# Revit family: 563622030037
name_source: partatom
category: Plumbing Fixtures
revit_build: Autodesk Revit 2017 (Build: 20190508_0315(x64)
units: mm (PartAtom-declared; Revit-internal decimal feet)

## family parameters
Always vertical = Yes
Cut with Voids When Loaded = No
OmniClass Number = 23.45.55.00
OmniClass Title = Sanitary Faucets, Wastes
Part Type = Normal
Room Calculation Point = No
Round Connector Dimension = Use Diameter
Shared = No
Work Plane-Based = No

## types (1)
- 563622030037 Washbasin faucet
    AssetType = Fixed
    BIMObjectName = 563622030037
    BodyMaterial = Brass
    Brand = Hansa
    Catalog Drawing URL = http://static.hansa.com
    Category = Bathroom
    Class = Single lever
    CloseOffRating = 0
    Color = Chrome
    Connection Size = G1/2
    ConvergoRefNr = 0087-1909-0142-FI
    Customs Code = 84818011
    DN Size = DN15
    Dimension Drawing URL = http://static.hansa.com
    DurationUnit = Year
    EAN Number = 4057304012068
    EN Standard = EN 817
    Extensions = Without popup waste
    FDV Document URL = http://www.hansa.com
    FaucetMainMaterial = Brass
    Features = Single lever
    Finish = Polished
    Flow Drawing URL = http://static.hansa.com
    Flow Rate At 300kPa With Flow Controller = 0.1 L/s
    FlowCoefficient = 0
    Group = Washbasin faucets
    IfcExportAs = IfcValveType
    IfcExportType = FAUCET
    InletConnectionSize = 10 mm  [stored 0.0328084 ft]
    Installation Type = Deck mounted
    Installation and Maintenance = http://static.hansa.com
    Lever Handle = Lever with H+C symbol
    ManufacterURL = http://www.hansa.com
    Manufacturer = Hansa
    ManufacturerName = Hansa
    Market = INT;AUS
    Material = Brass
    Max. Hot Water Supply = 90 °C
    Model = 563622030037 Washbasin faucet
    ModelReference = 563622030037
    Mounting Holes = 1 mounting hole
    NBSDescription = Water supply fittings for baths
    NBSReference = 45-35-70/315
    Name = 563622030037 Washbasin faucet
    Name_en = 563622030037 Washbasin faucet
    Noise Class = I (ISO 3822)
    NominalDepth = 137 mm
    NominalHeight = 136 mm
    NominalWidth = 49 mm
    Package Weight = 1.330 kg
    Package external Dimensions = 540 x 146 x 59
    Pipes = Flexible inlet pipes
    Product Code = 563622030037
    Product Datasheet = http://www.hansa.com
    Product Family = HANSAPALENO
    Product Image URL = http://static.hansa.com
    Product URL = http://static.hansa.com
    Projection = 102 mm
    Shape = Sculptured
    Size = 50x135x135 mm
    Spare Parts = http://static.hansa.com
    Spout Type = Fixed spout
    URL Global Mark = http://static.hansa.com
    Uniclass2 = Pr_40_20_87_07
    Uniclass2015Description = Bath manual water supply sets
    Uniclass2015Reference = Pr_40_30_96_07
    Version = 1
    VersionDate = 30/07/2019
    WarrantyDescription = http://warranty.hansa.com
    WarrantyDurationUnit = Year
    WorkingPressure = 50 - 1000 kPa

note: [stored X ft] marks values corroborated as IEEE doubles in the binary element streams (Revit-internal decimal feet)

## geometry (parser evidence)
native form markers: Sweep x6
no freeform markers — native parametric forms only
